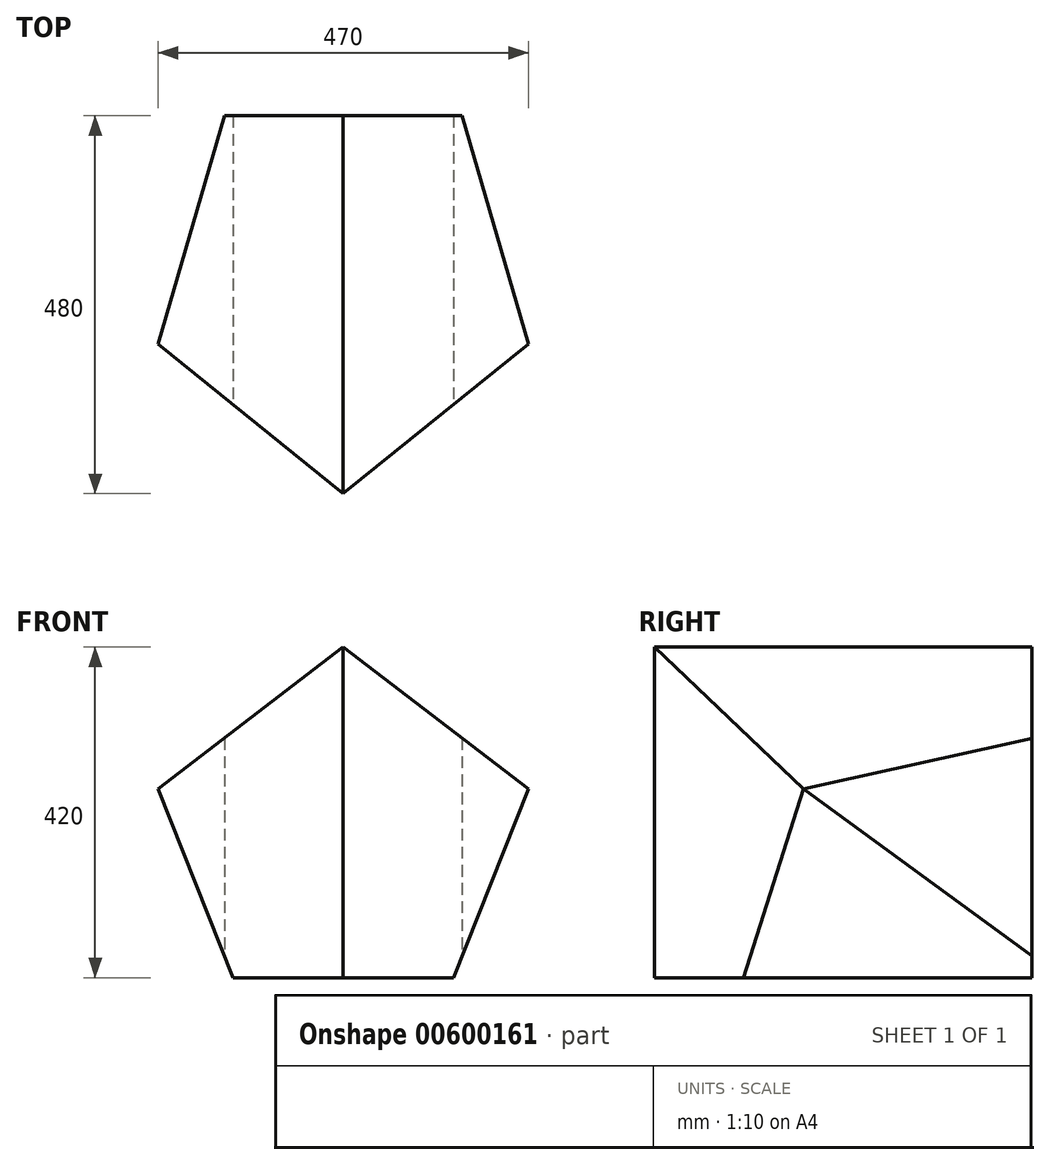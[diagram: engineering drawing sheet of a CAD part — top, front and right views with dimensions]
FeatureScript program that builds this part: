
annotation { "Feature Type Name" : "Feature", "Feature Type Description" : "" }
export const myFeature = defineFeature(function(context is Context, id is Id, definition is map)
    precondition{}
    {
        {
            var Q0;
            Q0=qCreatedBy(makeId("Front.planeOp"),FACE);
            var sketch = newSketch(context, id + "F0", { "sketchPlane" : qUnion([Q0])});
            skLineSegment(sketch, "E0.bottom", {"start": v(235, 210) * mm, "end": v(-235, 210) * mm});
            skLineSegment(sketch, "E0.top", {"start": v(235, -210) * mm, "end": v(-235, -210) * mm});
            skLineSegment(sketch, "E0.left", {"start": v(235, 210) * mm, "end": v(235, -210) * mm});
            skLineSegment(sketch, "E0.right", {"start": v(-235, 210) * mm, "end": v(-235, -210) * mm});
            skPoint(sketch, "E0.middle", {"position": v(0, 0) * mm});
            skSolve(sketch);
        }
        {
            var Q0;
            Q0=makeQuery(id+"F0.imprint","IMPRINT",FACE,{"disambiguationData":[TD([[makeQuery(id+"F0.imprint","IMPRINT",EDGE,{"derivedFrom":sQuery(id+"F0.wireOp",EDGE,"E0.bottom")}),1.0]])]});
            extrude(context, id + "F1", {"entities" : qUnion([Q0]), "endBound" : BoundingType.SYMMETRIC, "depth" : 480 * mm, "offsetDistance" : 25.4 * mm});
        }
        {
            var Q0;
            Q0=makeQuery(id+"F1.opExtrude","CAP_FACE",FACE,{"disambiguationData":[OSD([sQuery(id+"F0.wireOp",EDGE,"E0.bottom"),sQuery(id+"F0.wireOp",EDGE,"E0.top"),sQuery(id+"F0.wireOp",EDGE,"E0.left"),sQuery(id+"F0.wireOp",EDGE,"E0.right")])],"isStart":false});
            var sketch = newSketch(context, id + "F2", { "sketchPlane" : qUnion([Q0])});
            skLineSegment(sketch, "E1", {"start": v(140, -210) * mm, "end": v(235, 30) * mm});
            skLineSegment(sketch, "E2", {"start": v(235, 30) * mm, "end": v(235, 30) * mm});
            skLineSegment(sketch, "E3", {"start": v(0, 210) * mm, "end": v(235, 30) * mm});
            skLineSegment(sketch, "E4", {"start": v(-140, -210) * mm, "end": v(-235, 30) * mm});
            skLineSegment(sketch, "E5", {"start": v(-235, 30) * mm, "end": v(0, 210) * mm});
            skLineSegment(sketch, "E6", {"start": v(-140, -210) * mm, "end": v(-235, -210) * mm});
            skLineSegment(sketch, "E7", {"start": v(140, -210) * mm, "end": v(235, -210) * mm});
            skSolve(sketch);
        }
        {
            var Q0;
            {var subQ0=sQuery(id+"F2.wireOp",EDGE,"E3");Q0=makeQuery(id+"F2.imprint","IMPRINT",FACE,{"disambiguationData":[TD([[makeQuery(id+"F2.imprint","IMPRINT",EDGE,{"derivedFrom":subQ0}),1.0]])]});}
            var Q1;
            {var subQ0=sQuery(id+"F2.wireOp",EDGE,"E1");Q1=makeQuery(id+"F2.imprint","IMPRINT",FACE,{"disambiguationData":[TD([[makeQuery(id+"F2.imprint","IMPRINT",EDGE,{"derivedFrom":subQ0}),-1.0]])]});}
            var Q2;
            {var subQ0=sQuery(id+"F2.wireOp",EDGE,"E4");Q2=makeQuery(id+"F2.imprint","IMPRINT",FACE,{"disambiguationData":[TD([[makeQuery(id+"F2.imprint","IMPRINT",EDGE,{"derivedFrom":subQ0}),1.0]])]});}
            var Q3;
            {var subQ0=sQuery(id+"F2.wireOp",EDGE,"E5");Q3=makeQuery(id+"F2.imprint","IMPRINT",FACE,{"disambiguationData":[TD([[makeQuery(id+"F2.imprint","IMPRINT",EDGE,{"derivedFrom":subQ0}),1.0]])]});}
            extrude(context, id + "F3", {"entities" : qUnion([Q0, Q1, Q2, Q3]), "operationType" : NewBodyOperationType.REMOVE, "endBound" : BoundingType.THROUGH_ALL, "oppositeDirection" : true, "depth" : 25.4 * mm, "offsetDistance" : 25.4 * mm});
        }
        {
            var Q0;
            Q0=makeQuery(id+"F1.opExtrude","SWEPT_FACE",FACE,{"disambiguationData":[OSD([sQuery(id+"F0.wireOp",EDGE,"E0.top")])]});
            var sketch = newSketch(context, id + "F4", { "sketchPlane" : qUnion([Q0])});
            skLineSegment(sketch, "E8", {"start": v(151.04, -240) * mm, "end": v(235, 50.18) * mm});
            skLineSegment(sketch, "E9", {"start": v(235, 50.18) * mm, "end": v(235, 50.18) * mm});
            skLineSegment(sketch, "E10", {"start": v(0, 240) * mm, "end": v(235, 50.18) * mm});
            skLineSegment(sketch, "E11", {"start": v(-151.04, -240) * mm, "end": v(-235, 50.18) * mm});
            skLineSegment(sketch, "E12", {"start": v(-235, 50.18) * mm, "end": v(0, 240) * mm});
            skLineSegment(sketch, "E13", {"start": v(-151.04, -240) * mm, "end": v(151.04, -240) * mm});
            skLineSegment(sketch, "E14", {"start": v(-235, 50.18) * mm, "end": v(-235, 240) * mm});
            skLineSegment(sketch, "E15", {"start": v(-235, 240) * mm, "end": v(0, 240) * mm});
            skLineSegment(sketch, "E16", {"start": v(0, 240) * mm, "end": v(235, 240) * mm});
            skLineSegment(sketch, "E17", {"start": v(235, 50.18) * mm, "end": v(235, 240) * mm});
            skLineSegment(sketch, "E18", {"start": v(151.04, -240) * mm, "end": v(235, -240) * mm});
            skLineSegment(sketch, "E19", {"start": v(235, -240) * mm, "end": v(235, 50.18) * mm});
            skLineSegment(sketch, "E20", {"start": v(-151.04, -240) * mm, "end": v(-235, -240) * mm});
            skLineSegment(sketch, "E21", {"start": v(-235, -240) * mm, "end": v(-235, 50.18) * mm});
            skSolve(sketch);
        }
        {
            var Q0;
            {var subQ0=sQuery(id+"F4.wireOp",EDGE,"E17");Q0=makeQuery(id+"F4.imprint","IMPRINT",FACE,{"disambiguationData":[TD([[makeQuery(id+"F4.imprint","IMPRINT",EDGE,{"derivedFrom":subQ0}),1.0]])]});}
            var Q1;
            {var subQ0=sQuery(id+"F4.wireOp",EDGE,"E16");var subQ1=sQuery(id+"F4.wireOp",EDGE,"E10");var subQ2=makeQuery(id+"F4.imprint","INTERSECT",VERTEX,{"derivedFrom":[subQ1,sQuery(id+"F4.wireOp",EDGE,"E12"),sQuery(id+"F4.wireOp",EDGE,"E15"),subQ0]});Q1=makeQuery(id+"F4.imprint","IMPRINT",FACE,{"disambiguationData":[TD([[makeQuery(id+"F4.imprint","IMPRINT",EDGE,{"disambiguationData":[TD([[subQ2,-1.0]])],"derivedFrom":subQ1}),1.0]])]});}
            var Q2;
            Q2=makeQuery(id+"F4.imprint","IMPRINT",FACE,{"disambiguationData":[TD([[makeQuery(id+"F4.imprint","IMPRINT",EDGE,{"derivedFrom":sQuery(id+"F4.wireOp",EDGE,"E8")}),-1.0]])]});
            var Q3;
            Q3=makeQuery(id+"F4.imprint","IMPRINT",FACE,{"disambiguationData":[TD([[makeQuery(id+"F4.imprint","IMPRINT",EDGE,{"derivedFrom":sQuery(id+"F4.wireOp",EDGE,"E11")}),1.0]])]});
            var Q4;
            {var subQ0=sQuery(id+"F4.wireOp",EDGE,"E14");Q4=makeQuery(id+"F4.imprint","IMPRINT",FACE,{"disambiguationData":[TD([[makeQuery(id+"F4.imprint","IMPRINT",EDGE,{"derivedFrom":subQ0}),-1.0]])]});}
            var Q5;
            {var subQ0=sQuery(id+"F4.wireOp",EDGE,"E15");var subQ1=sQuery(id+"F4.wireOp",EDGE,"E12");var subQ2=makeQuery(id+"F4.imprint","INTERSECT",VERTEX,{"derivedFrom":[sQuery(id+"F4.wireOp",EDGE,"E10"),subQ1,subQ0,sQuery(id+"F4.wireOp",EDGE,"E16")]});Q5=makeQuery(id+"F4.imprint","IMPRINT",FACE,{"disambiguationData":[TD([[makeQuery(id+"F4.imprint","IMPRINT",EDGE,{"disambiguationData":[TD([[subQ2,1.0]])],"derivedFrom":subQ1}),1.0]])]});}
            extrude(context, id + "F5", {"entities" : qUnion([Q0, Q1, Q2, Q3, Q4, Q5]), "operationType" : NewBodyOperationType.REMOVE, "endBound" : BoundingType.THROUGH_ALL, "oppositeDirection" : true, "depth" : 25.4 * mm, "offsetDistance" : 25.4 * mm});
        }
    });
